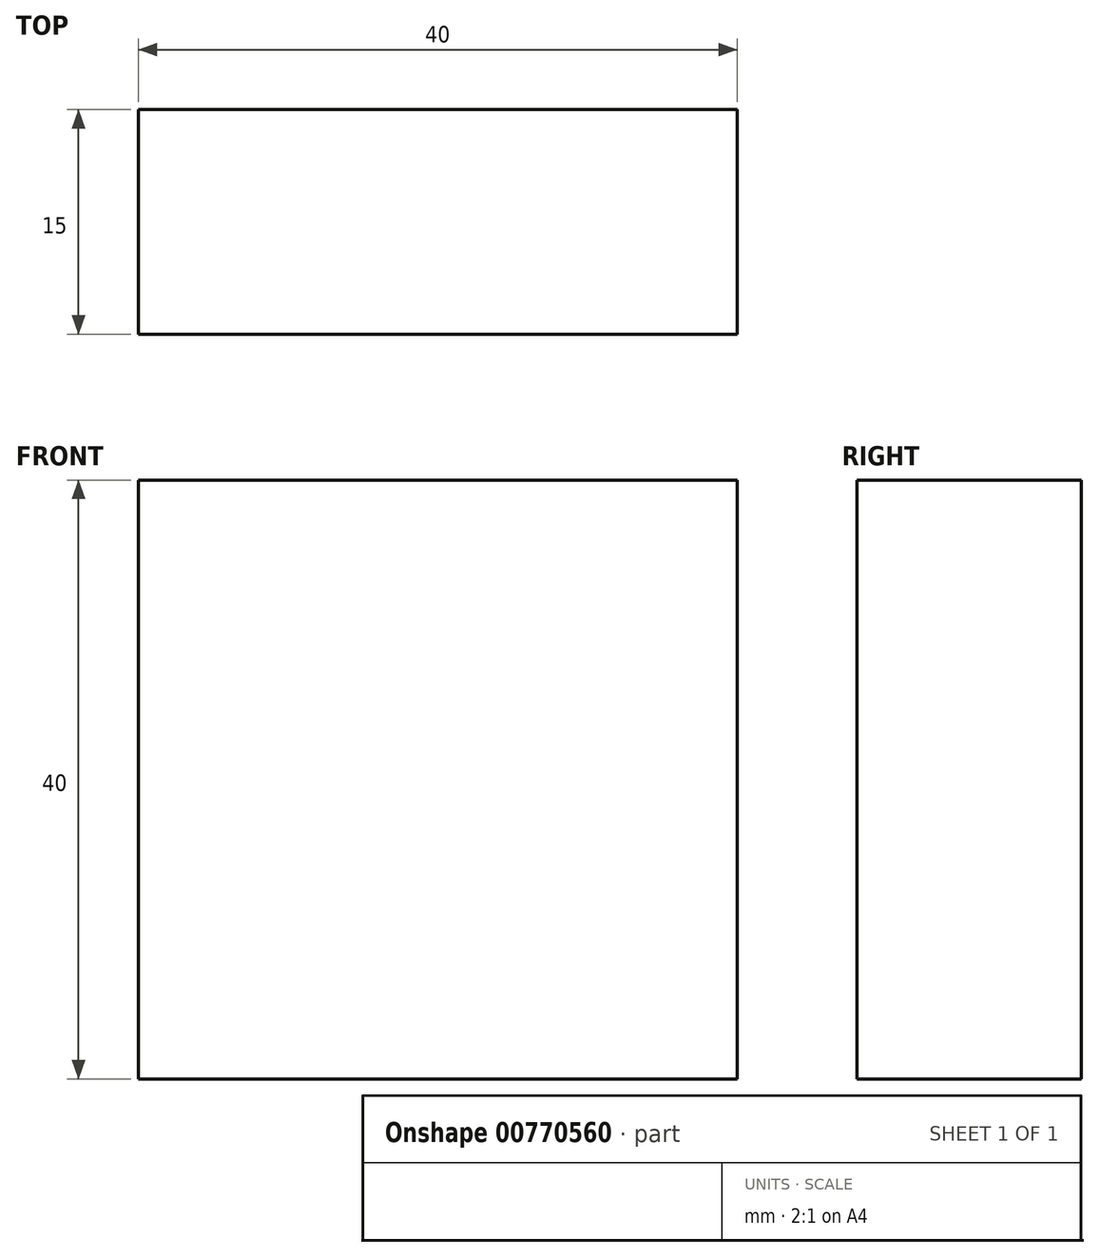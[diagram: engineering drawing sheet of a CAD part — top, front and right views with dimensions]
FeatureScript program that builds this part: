
annotation { "Feature Type Name" : "Feature", "Feature Type Description" : "" }
export const myFeature = defineFeature(function(context is Context, id is Id, definition is map)
    precondition{}
    {
        {
            var Q0;
            Q0=qCreatedBy(makeId("Top.planeOp"),FACE);
            var sketch = newSketch(context, id + "F0", { "sketchPlane" : qUnion([Q0])});
            skLineSegment(sketch, "E0.bottom", {"start": v(0, 0) * mm, "end": v(-40, 0) * mm});
            skLineSegment(sketch, "E0.top", {"start": v(0, 15) * mm, "end": v(-40, 15) * mm});
            skLineSegment(sketch, "E0.left", {"start": v(0, 0) * mm, "end": v(0, 15) * mm});
            skLineSegment(sketch, "E0.right", {"start": v(-40, 0) * mm, "end": v(-40, 15) * mm});
            skSolve(sketch);
        }
        {
            var Q0;
            Q0 = qSketchRegion(id + "F0", true);
            extrude(context, id + "F1", {"entities" : qUnion([Q0]), "depth" : 40 * mm, "offsetDistance" : 25 * mm});
        }
    });
